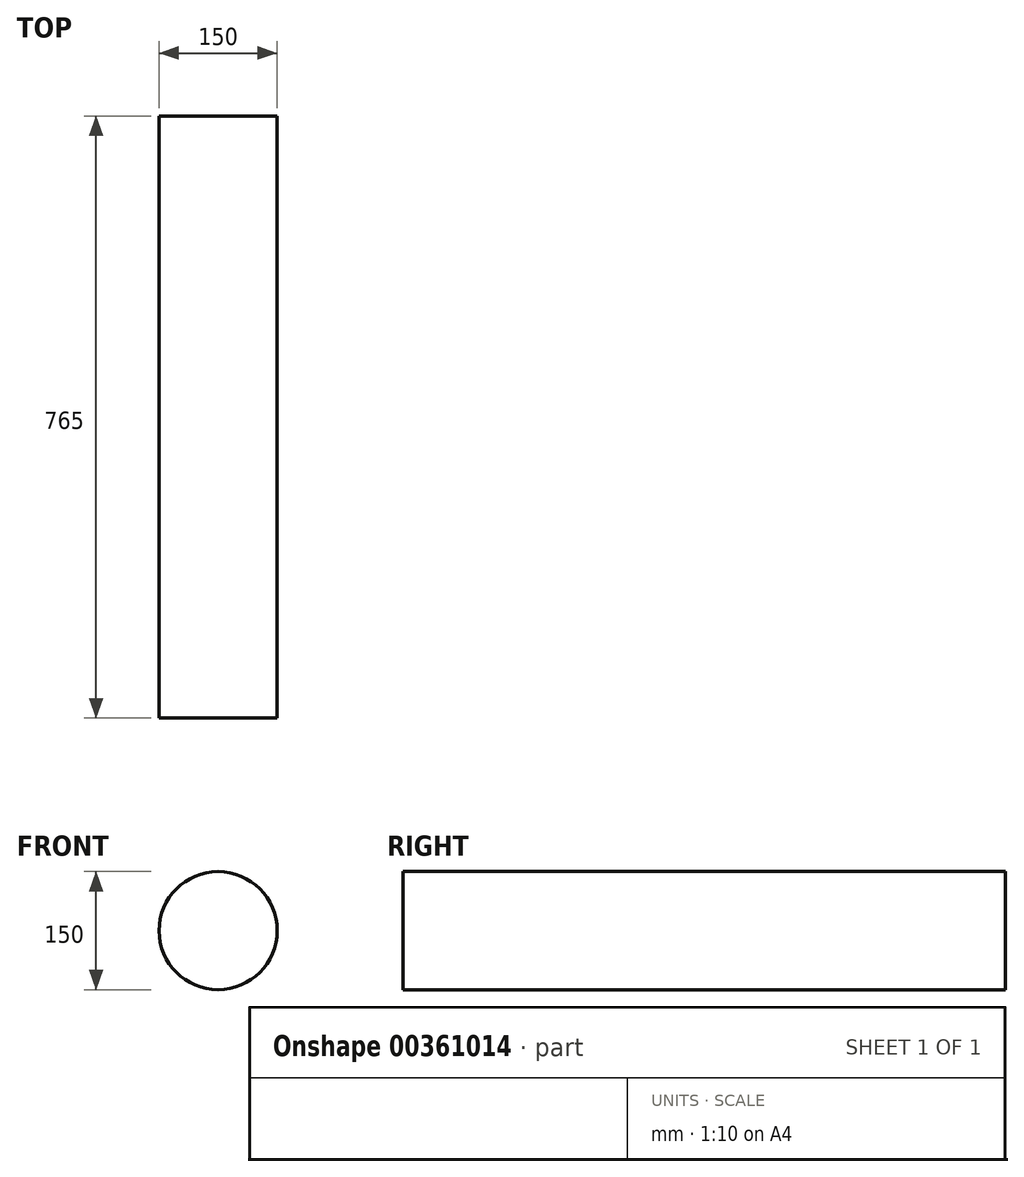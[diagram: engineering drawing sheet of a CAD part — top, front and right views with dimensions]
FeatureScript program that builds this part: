
annotation { "Feature Type Name" : "Feature", "Feature Type Description" : "" }
export const myFeature = defineFeature(function(context is Context, id is Id, definition is map)
    precondition{}
    {
        {
            var Q0;
            Q0=qCreatedBy(makeId("Front.planeOp"),FACE);
            var sketch = newSketch(context, id + "F0", { "sketchPlane" : qUnion([Q0])});
            skCircle(sketch, "E0", {"center": v(0, 0) * mm, "radius": 75 * mm});
            skSolve(sketch);
        }
        {
            var Q0;
            Q0=makeQuery(id+"F0.imprint","IMPRINT",FACE,{"disambiguationData":[TD([[makeQuery(id+"F0.imprint","IMPRINT",EDGE,{"derivedFrom":sQuery(id+"F0.wireOp",EDGE,"E0")}),1.0]])]});
            extrude(context, id + "F1", {"entities" : qUnion([Q0]), "endBound" : BoundingType.SYMMETRIC, "depth" : 765 * mm});
        }
    });
